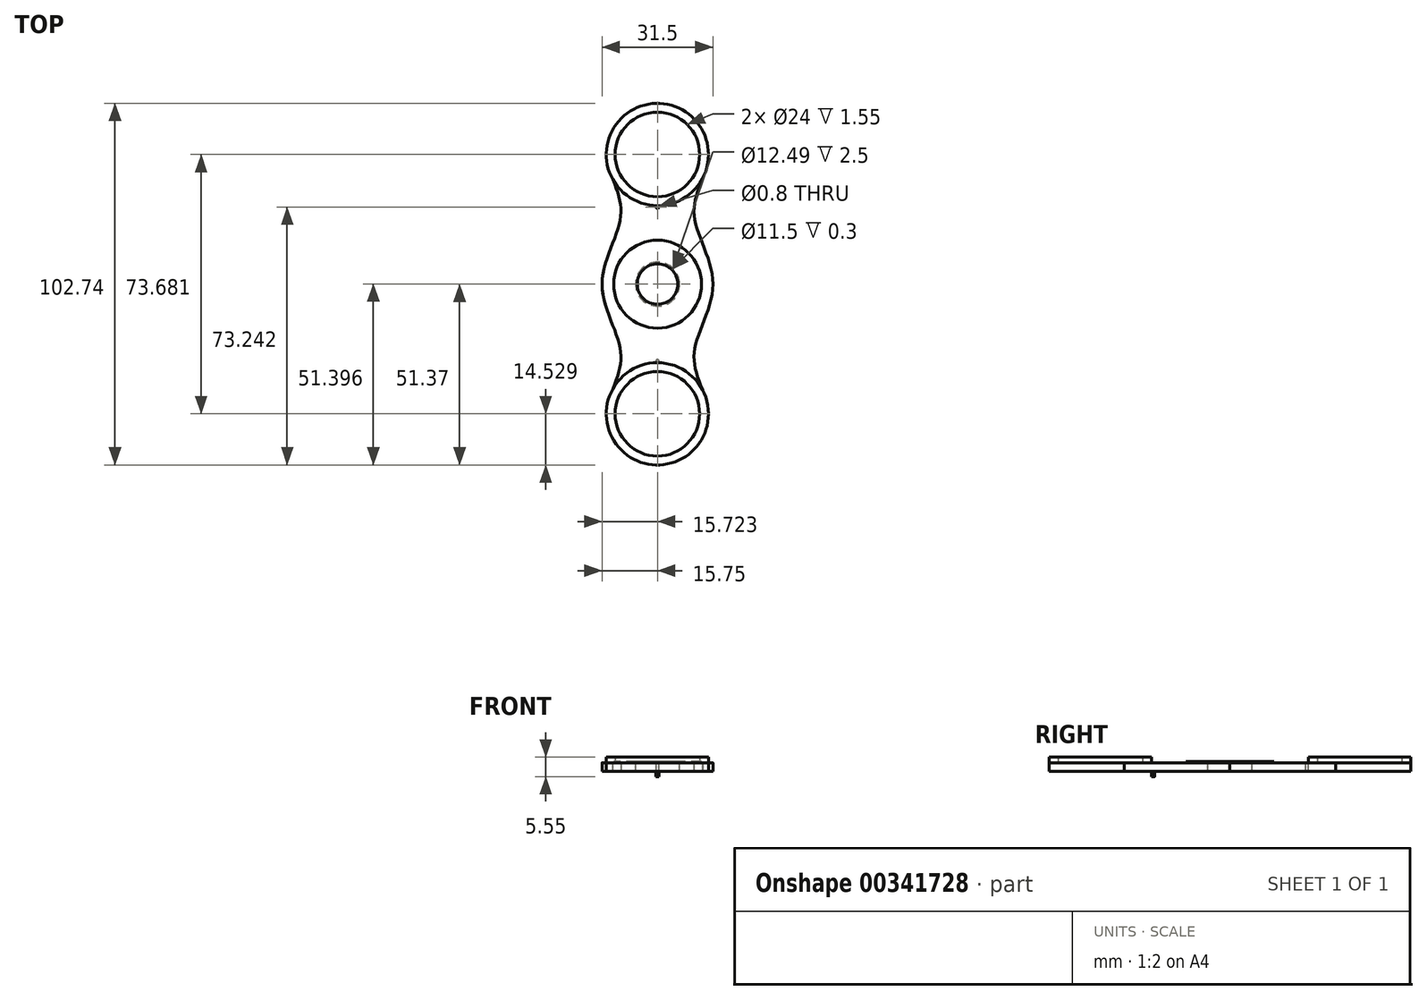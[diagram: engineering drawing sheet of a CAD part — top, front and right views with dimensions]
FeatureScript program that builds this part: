
annotation { "Feature Type Name" : "Feature", "Feature Type Description" : "" }
export const myFeature = defineFeature(function(context is Context, id is Id, definition is map)
    precondition{}
    {
        {
            var Q0;
            Q0=qCreatedBy(makeId("Top.planeOp"),FACE);
            var sketch = newSketch(context, id + "F0", { "sketchPlane" : qUnion([Q0])});
            skCircle(sketch, "E0", {"center": v(-0.03, 36.84) * mm, "radius": 14.5 * mm});
            skPoint(sketch, "E0.first.point", {"position": v(-14.52, 37.09) * mm});
            skPoint(sketch, "E0.second.point", {"position": v(14.47, 36.66) * mm});
            skPoint(sketch, "E0.third.point", {"position": v(0, 22.34) * mm});
            skSolve(sketch);
        }
        {
            var Q0;
            Q0=makeQuery(id+"F0.imprint","IMPRINT",FACE,{"disambiguationData":[TD([[makeQuery(id+"F0.imprint","IMPRINT",EDGE,{"derivedFrom":sQuery(id+"F0.wireOp",EDGE,"E0")}),1.0]])]});
            extrude(context, id + "F1", {"entities" : qUnion([Q0]), "depth" : 2.5 * mm});
        }
        {
            var Q0;
            Q0=makeQuery(id+"F1.opExtrude","SWEPT_BODY",BODY,{"disambiguationData":[OSD([sQuery(id+"F0.wireOp",EDGE,"E0")])]});
            var Q1;
            Q1=makeQuery(id+"F1.opExtrude","CAP_FACE",FACE,{"disambiguationData":[OSD([sQuery(id+"F0.wireOp",EDGE,"E0")])],"isStart":false});
            var Q2;
            Q2=qCreatedBy(makeId("Front.planeOp"),FACE);
            mirror(context, id + "F2", {"operationType" : NewBodyOperationType.ADD, "entities" : qUnion([Q0]), "faces" : qUnion([Q1]), "mirrorPlane" : qUnion([Q2])});
        }
        {
            var Q0;
            Q0=qCreatedBy(makeId("Top.planeOp"),FACE);
            var sketch = newSketch(context, id + "F3", { "sketchPlane" : qUnion([Q0])});
            skFitSpline(sketch, "E1", {"points": [v(-12.09, 28.75) * mm, v(-10.3, 16.8) * mm, v(-15.75, 0) * mm, v(-10.67, -17.86) * mm, v(-12.82, -30.03) * mm], "startDerivative": vector(31.75, -58.25) * mm, "endDerivative": vector(-25.02, -61.58) * mm});
            skFitSpline(sketch, "E2.MirrorCS", {"points": [v(12.09, 28.75) * mm, v(10.3, 16.8) * mm, v(15.75, 0) * mm, v(10.67, -17.86) * mm, v(12.82, -30.03) * mm], "startDerivative": vector(-31.75, -58.25) * mm, "endDerivative": vector(25.02, -61.58) * mm});
            skLineSegment(sketch, "E3", {"start": v(-12.09, 28.75) * mm, "end": v(12.09, 28.75) * mm});
            skLineSegment(sketch, "E4", {"start": v(-12.82, -30.03) * mm, "end": v(12.82, -30.03) * mm});
            skSolve(sketch);
        }
        {
            var Q0;
            Q0=makeQuery(id+"F3.imprint","IMPRINT",FACE,{"disambiguationData":[TD([[makeQuery(id+"F3.imprint","IMPRINT",EDGE,{"derivedFrom":sQuery(id+"F3.wireOp",EDGE,"E1")}),1.0]])]});
            extrude(context, id + "F4", {"entities" : qUnion([Q0]), "operationType" : NewBodyOperationType.ADD, "depth" : 2.5 * mm});
        }
        {
            var Q0;
            {var subQ0=makeQuery(id+"F1.opExtrude","CAP_FACE",FACE,{"disambiguationData":[OSD([sQuery(id+"F0.wireOp",EDGE,"E0")])],"isStart":false});Q0=makeQuery(id+"F4.boolean.opBoolean","MERGE",FACE,{"derivedFrom":[subQ0,makeQuery(id+"F2.opPattern","COPY",FACE,{"derivedFrom":subQ0,"instanceName":"1"}),makeQuery(id+"F4.opExtrude","CAP_FACE",FACE,{"disambiguationData":[OSD([sQuery(id+"F3.wireOp",EDGE,"E1"),sQuery(id+"F3.wireOp",EDGE,"E2.MirrorCS"),sQuery(id+"F3.wireOp",EDGE,"E3"),sQuery(id+"F3.wireOp",EDGE,"E4")])],"isStart":false})]});}
            var sketch = newSketch(context, id + "F5", { "sketchPlane" : qUnion([Q0])});
            skCircle(sketch, "E5", {"center": v(-0.03, 36.84) * mm, "radius": 14.52 * mm});
            skCircle(sketch, "E6", {"center": v(-0.03, -36.84) * mm, "radius": 14.5 * mm});
            skSolve(sketch);
        }
        {
            var Q0;
            Q0=qSketchRegion(id+"F5",true);
            extrude(context, id + "F6", {"entities" : qUnion([Q0]), "operationType" : NewBodyOperationType.ADD, "depth" : 1.55 * mm});
        }
        {
            var Q0;
            Q0=makeQuery(id+"F6.opExtrude","CAP_FACE",FACE,{"disambiguationData":[OSD([sQuery(id+"F5.wireOp",EDGE,"E5")])],"isStart":false});
            var Q1;
            Q1=makeQuery(id+"F6.opExtrude","CAP_FACE",FACE,{"disambiguationData":[OSD([sQuery(id+"F5.wireOp",EDGE,"E6")])],"isStart":false});
            shell(context, id + "F7", {"entities" : qUnion([Q0, Q1]), "thickness" : 2.5 * mm});
        }
        {
            var Q0;
            Q0=makeQuery(id+"F6.opExtrude","CAP_FACE",FACE,{"disambiguationData":[OSD([sQuery(id+"F5.wireOp",EDGE,"E6")])],"isStart":false});
            shell(context, id + "F8", {"entities" : qUnion([Q0]), "thickness" : 2.5 * mm});
        }
        {
            var Q0;
            Q0=qSketchRegion(id+"F5",true);
            var sketch = newSketch(context, id + "F9", { "sketchPlane" : qUnion([Q0])});
            skSolve(sketch);
        }
        {
            var Q0;
            Q0=makeQuery(id+"F5.imprint","IMPRINT",FACE,{"disambiguationData":[TD([[makeQuery(id+"F5.imprint","IMPRINT",EDGE,{"disambiguationData":[OD(0.0)],"derivedFrom":sQuery(id+"F5.wireOp",EDGE,"E6")}),-1.0]])]});
            var sketch = newSketch(context, id + "F10", { "sketchPlane" : qUnion([Q0])});
            skLineSegment(sketch, "E7.bottom", {"start": v(6.67, 23.56) * mm, "end": v(-5.88, 23.56) * mm});
            skLineSegment(sketch, "E7.top", {"start": v(6.67, 21.32) * mm, "end": v(-5.88, 21.32) * mm});
            skLineSegment(sketch, "E7.left", {"start": v(6.67, 23.56) * mm, "end": v(6.67, 21.32) * mm});
            skLineSegment(sketch, "E7.right", {"start": v(-5.88, 23.56) * mm, "end": v(-5.88, 21.32) * mm});
            skSolve(sketch);
        }
        {
            var Q0;
            Q0=makeQuery(id+"F1.opExtrude","SWEPT_BODY",BODY,{"disambiguationData":[OSD([sQuery(id+"F0.wireOp",EDGE,"E0")])]});
            var Q1;
            Q1=qCreatedBy(makeId("Front.planeOp"),FACE);
            mirror(context, id + "F11", {"operationType" : NewBodyOperationType.ADD, "entities" : qUnion([Q0]), "mirrorPlane" : qUnion([Q1])});
        }
        {
            var Q0;
            Q0=makeQuery(id+"F5.imprint","IMPRINT",FACE,{"disambiguationData":[TD([[makeQuery(id+"F5.imprint","IMPRINT",EDGE,{"disambiguationData":[OD(0.0)],"derivedFrom":sQuery(id+"F5.wireOp",EDGE,"E6")}),-1.0]])]});
            var sketch = newSketch(context, id + "F12", { "sketchPlane" : qUnion([Q0])});
            skCircle(sketch, "E8", {"center": v(0, 0) * mm, "radius": 12.5 * mm});
            skSolve(sketch);
        }
        {
            var Q0;
            Q0=qSketchRegion(id+"F12",true);
            var sketch = newSketch(context, id + "F13", { "sketchPlane" : qUnion([Q0])});
            skCircle(sketch, "E9", {"center": v(0.02, 0) * mm, "radius": 12.49 * mm});
            skPoint(sketch, "E9.first.point", {"position": v(-8.63, 9) * mm});
            skPoint(sketch, "E9.second.point", {"position": v(-6.8, -10.46) * mm});
            skPoint(sketch, "E9.third.point", {"position": v(12.49, 0.65) * mm});
            skSolve(sketch);
        }
        {
            var Q0;
            Q0=sQuery(id+"F12.wireOp",VERTEX,"E8.center");
            var Q1;
            Q1=makeQuery(id+"F1.opExtrude","SWEPT_BODY",BODY,{"disambiguationData":[OSD([sQuery(id+"F0.wireOp",EDGE,"E0")])]});
            hole(context, id + "F14", {"style" : HoleStyle.SIMPLE, "endStyle" : HoleEndStyle.THROUGH, "holeDiameter" : 12.5 * mm, "isTappedThrough" : true, "tappedDepth" : 12 * mm, "tapClearance" : 3, "locations" : qUnion([Q0]), "scope" : qUnion([Q1])});
        }
        {
            var Q0;
            {var subQ24=sQuery(id+"F10.wireOp",EDGE,"E7.top");Q0=makeQuery(id+"F10.imprint","IMPRINT",FACE,{"disambiguationData":[TD([[makeQuery(id+"F10.imprint","IMPRINT",EDGE,{"derivedFrom":subQ24}),1.0]])]});}
            var sketch = newSketch(context, id + "F15", { "sketchPlane" : qUnion([Q0])});
            skPoint(sketch, "E10", {"position": v(0, 0.03) * mm});
            skPoint(sketch, "E11", {"position": v(0, 12.52) * mm});
            skSolve(sketch);
        }
        {
            var Q0;
            {var subQ1=sQuery(id+"F10.wireOp",EDGE,"E7.top");Q0=makeQuery(id+"F10.imprint","IMPRINT",FACE,{"disambiguationData":[TD([[makeQuery(id+"F10.imprint","IMPRINT",EDGE,{"derivedFrom":subQ1}),-1.0]])]});}
            var sketch = newSketch(context, id + "F16", { "sketchPlane" : qUnion([Q0])});
            skPoint(sketch, "E12", {"position": v(0, 21.87) * mm});
            skSolve(sketch);
        }
        {
            var Q0;
            Q0=sQuery(id+"F16.wireOp",VERTEX,"E12");
            var Q1;
            Q1=makeQuery(id+"F1.opExtrude","SWEPT_BODY",BODY,{"disambiguationData":[OSD([sQuery(id+"F0.wireOp",EDGE,"E0")])]});
            hole(context, id + "F17", {"style" : HoleStyle.SIMPLE, "endStyle" : HoleEndStyle.THROUGH, "holeDiameter" : .8 * mm, "isTappedThrough" : true, "tappedDepth" : 12 * mm, "tapClearance" : 3, "locations" : qUnion([Q0]), "scope" : qUnion([Q1])});
        }
        {
            var Q0;
            Q0=makeQuery(id+"F5.imprint","IMPRINT",FACE,{"disambiguationData":[TD([[makeQuery(id+"F5.imprint","IMPRINT",EDGE,{"disambiguationData":[OD(0.0)],"derivedFrom":sQuery(id+"F5.wireOp",EDGE,"E6")}),-1.0]])]});
            var sketch = newSketch(context, id + "F18", { "sketchPlane" : qUnion([Q0])});
            skPoint(sketch, "E13", {"position": v(0, -21.87) * mm});
            skCircle(sketch, "E14", {"center": v(0, -21.87) * mm, "radius": 0.45 * mm});
            skPoint(sketch, "E15", {"position": v(0.44, -21.88) * mm});
            skSolve(sketch);
        }
        {
            var Q0;
            Q0=qSketchRegion(id+"F13",true);
            extrude(context, id + "F19", {"entities" : qUnion([Q0]), "operationType" : NewBodyOperationType.ADD, "depth" : .3 * mm});
        }
        {
            var Q0;
            Q0=sQuery(id+"F15.wireOp",VERTEX,"E10");
            var Q1;
            Q1=makeQuery(id+"F1.opExtrude","SWEPT_BODY",BODY,{"disambiguationData":[OSD([sQuery(id+"F0.wireOp",EDGE,"E0")])]});
            hole(context, id + "F20", {"style" : HoleStyle.SIMPLE, "endStyle" : HoleEndStyle.THROUGH, "oppositeDirection" : true, "holeDiameter" : 11.5 * mm, "isTappedThrough" : true, "tappedDepth" : 12 * mm, "tapClearance" : 3, "locations" : qUnion([Q0]), "scope" : qUnion([Q1])});
        }
        {
            var Q0;
            Q0=makeQuery(id+"F18.imprint","IMPRINT",FACE,{"disambiguationData":[TD([[makeQuery(id+"F18.imprint","IMPRINT",EDGE,{"derivedFrom":sQuery(id+"F18.wireOp",EDGE,"E14")}),1.0]])]});
            extrude(context, id + "F21", {"entities" : qUnion([Q0]), "operationType" : NewBodyOperationType.ADD, "oppositeDirection" : true, "depth" : 4 * mm});
        }
    });
